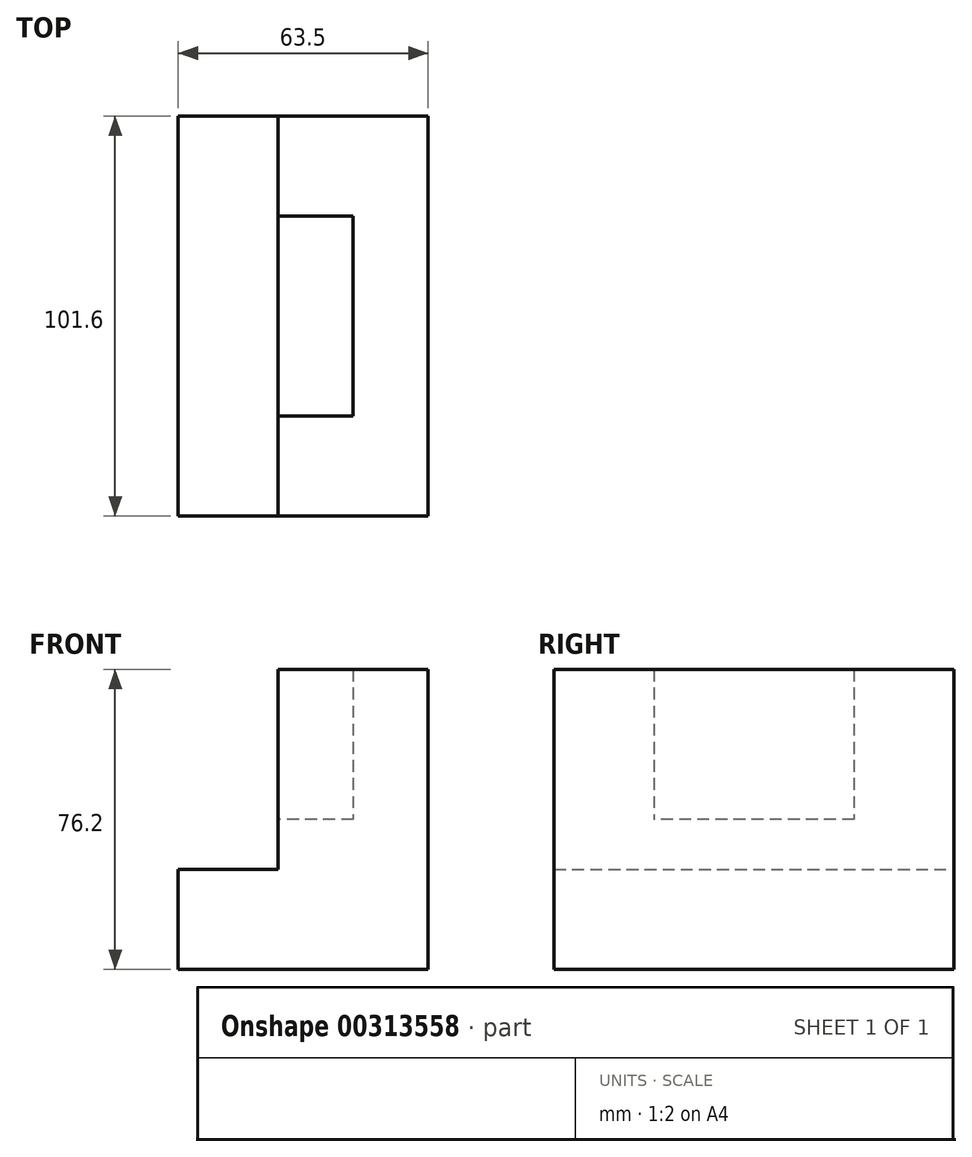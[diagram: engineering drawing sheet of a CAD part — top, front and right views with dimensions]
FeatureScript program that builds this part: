
annotation { "Feature Type Name" : "Feature", "Feature Type Description" : "" }
export const myFeature = defineFeature(function(context is Context, id is Id, definition is map)
    precondition{}
    {
        {
            var Q0;
            Q0=qCreatedBy(makeId("Front.planeOp"),FACE);
            var sketch = newSketch(context, id + "F0", { "sketchPlane" : qUnion([Q0])});
            skLineSegment(sketch, "E0", {"start": v(-29.9, -43.18) * mm, "end": v(33.6, -43.18) * mm});
            skLineSegment(sketch, "E1", {"start": v(33.6, -43.18) * mm, "end": v(33.6, 33.02) * mm});
            skLineSegment(sketch, "E2", {"start": v(33.6, 33.02) * mm, "end": v(-4.5, 33.02) * mm});
            skLineSegment(sketch, "E3", {"start": v(-4.5, 33.02) * mm, "end": v(-4.5, -17.78) * mm});
            skLineSegment(sketch, "E4", {"start": v(-4.5, -17.78) * mm, "end": v(-29.9, -17.78) * mm});
            skLineSegment(sketch, "E5", {"start": v(-29.9, -17.78) * mm, "end": v(-29.9, -43.18) * mm});
            skSolve(sketch);
        }
        {
            var Q0;
            Q0 = qSketchRegion(id + "F0", true);
            extrude(context, id + "F1", {"entities" : qUnion([Q0]), "depth" : 101.6 * mm});
        }
        {
            var Q0;
            Q0=makeQuery(id+"F1.opExtrude","SWEPT_FACE",FACE,{"disambiguationData":[OSD([sQuery(id+"F0.wireOp",EDGE,"E3")])]});
            var sketch = newSketch(context, id + "F2", { "sketchPlane" : qUnion([Q0])});
            skLineSegment(sketch, "E6.bottom", {"start": v(25.4, 33.02) * mm, "end": v(76.2, 33.02) * mm});
            skLineSegment(sketch, "E6.top", {"start": v(25.4, -5.08) * mm, "end": v(76.2, -5.08) * mm});
            skLineSegment(sketch, "E6.left", {"start": v(25.4, 33.02) * mm, "end": v(25.4, -5.08) * mm});
            skLineSegment(sketch, "E6.right", {"start": v(76.2, 33.02) * mm, "end": v(76.2, -5.08) * mm});
            skLineSegment(sketch, "E7.bottom", {"start": v(0, 33.02) * mm, "end": v(101.6, 33.02) * mm});
            skLineSegment(sketch, "E7.top", {"start": v(0, -17.78) * mm, "end": v(101.6, -17.78) * mm});
            skLineSegment(sketch, "E7.left", {"start": v(0, 33.02) * mm, "end": v(0, -17.78) * mm});
            skLineSegment(sketch, "E7.right", {"start": v(101.6, 33.02) * mm, "end": v(101.6, -17.78) * mm});
            skSolve(sketch);
        }
        {
            var Q0;
            Q0=makeQuery(id+"F2.imprint","IMPRINT",FACE,{"disambiguationData":[TD([[makeQuery(id+"F2.imprint","IMPRINT",EDGE,{"derivedFrom":sQuery(id+"F2.wireOp",EDGE,"E6.top")}),1.0]])]});
            extrude(context, id + "F3", {"entities" : qUnion([Q0]), "operationType" : NewBodyOperationType.REMOVE, "oppositeDirection" : true, "depth" : 19.05 * mm});
        }
    });
